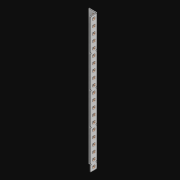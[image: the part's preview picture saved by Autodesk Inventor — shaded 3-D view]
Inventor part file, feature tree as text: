
AUTODESK INVENTOR PART (.ipt)
format: ipt  version: 2021 (Build 250183000, 183)  size: 1,229,824 bytes
history: native  units: in
note: dims shown in document units (in); Inventor stores cm internally (conversion verified against a paired STEP export)
features: extrude x44, other x42, sketch x4, pattern_linear x2, sheet_metal_op x1
ambient origin geometry x8: Origin, YZ Plane, XZ Plane, XY Plane, X Axis, Y Axis, Z Axis, Center Point
bodies: Solid1 (feature_tree)
feature tree (93):
  pattern_linear  "Rectangular Pattern1"  Spacing1=0.5in  [1 undecoded]
  pattern_linear  "Rectangular Pattern3"  Count1=21  [1 undecoded]
  extrude  "Extrusion1"  Depth=0.5in
  extrude  "Extrusion2"  Depth=0.5in
  sketch  "Sketch1"  dims[d0=0.182in]
  other  "Srf1"
  sketch  "Sketch3"  dims[d1=0.063in d2=0.0in]
  other  "Srf3"
  other  "Srf4"
  other  "Srf5"
  other  "Srf6"
  other  "Srf7"
  other  "Srf8"
  other  "Srf9"
  other  "Srf10"
  other  "Srf11"
  other  "Srf12"
  other  "Srf13"
  other  "Srf14"
  other  "Srf15"
  other  "Srf16"
  other  "Srf17"
  other  "Srf18"
  other  "Srf19"
  other  "Srf20"
  other  "Srf21"
  other  "Srf22"
  other  "Srf23"
  other  "Srf142"
  other  "Srf143"
  other  "Srf144"
  other  "Srf145"
  other  "Srf146"
  other  "Srf147"
  other  "Srf148"
  other  "Srf149"
  other  "Srf150"
  other  "Srf151"
  other  "Srf152"
  other  "Srf153"
  other  "Srf154"
  other  "Srf155"
  other  "Srf156"
  other  "Srf157"
  other  "Srf158"
  other  "Srf159"
  other  "Srf160"
  other  "Srf161"
  sketch  "Sketch4"  dims[d6=0.182in]
  sketch  "Sketch5"  dims[d7=0.063in d8=0.0in d11=0.5in d12=0.3937in d14=0.5in d18=8.2677in d20=0.5in d21=7.0in d22=0.0in d23=0.841in d24=0.0in]
  sheet_metal_op  "Fold1"
  extrude  "ExtrusionSrf1"  TaperAngle=0.0deg  [1 undecoded]
  extrude  "ExtrusionSrf3"  Depth=0.5in TaperAngle=0.0deg
  extrude  "ExtrusionSrf4"  [1 undecoded]
  extrude  "ExtrusionSrf5"  [1 undecoded]
  extrude  "ExtrusionSrf6"  [1 undecoded]
  extrude  "ExtrusionSrf7"  [1 undecoded]
  extrude  "ExtrusionSrf8"  [1 undecoded]
  extrude  "ExtrusionSrf9"  [1 undecoded]
  extrude  "ExtrusionSrf10"  [1 undecoded]
  extrude  "ExtrusionSrf11"  [1 undecoded]
  extrude  "ExtrusionSrf12"  [1 undecoded]
  extrude  "ExtrusionSrf13"  [1 undecoded]
  extrude  "ExtrusionSrf14"  [1 undecoded]
  extrude  "ExtrusionSrf15"  [1 undecoded]
  extrude  "ExtrusionSrf16"  [1 undecoded]
  extrude  "ExtrusionSrf17"  [1 undecoded]
  extrude  "ExtrusionSrf18"  [1 undecoded]
  extrude  "ExtrusionSrf19"  [1 undecoded]
  extrude  "ExtrusionSrf20"  [1 undecoded]
  extrude  "ExtrusionSrf21"  [1 undecoded]
  extrude  "ExtrusionSrf22"  [1 undecoded]
  extrude  "ExtrusionSrf23"  [1 undecoded]
  extrude  "ExtrusionSrf142"  [1 undecoded]
  extrude  "ExtrusionSrf143"  [1 undecoded]
  extrude  "ExtrusionSrf144"  [1 undecoded]
  extrude  "ExtrusionSrf145"  [1 undecoded]
  extrude  "ExtrusionSrf146"  [1 undecoded]
  extrude  "ExtrusionSrf147"  [1 undecoded]
  extrude  "ExtrusionSrf148"  [1 undecoded]
  extrude  "ExtrusionSrf149"  [1 undecoded]
  extrude  "ExtrusionSrf150"  [1 undecoded]
  extrude  "ExtrusionSrf151"  [1 undecoded]
  extrude  "ExtrusionSrf152"  [1 undecoded]
  extrude  "ExtrusionSrf153"  [1 undecoded]
  extrude  "ExtrusionSrf154"  [1 undecoded]
  extrude  "ExtrusionSrf155"  [1 undecoded]
  extrude  "ExtrusionSrf156"  [1 undecoded]
  extrude  "ExtrusionSrf157"  [1 undecoded]
  extrude  "ExtrusionSrf158"  [1 undecoded]
  extrude  "ExtrusionSrf159"  [1 undecoded]
  extrude  "ExtrusionSrf160"  [1 undecoded]
  extrude  "ExtrusionSrf161"  [1 undecoded]
note: 43 required parameter values undecoded (feature->parameter linkage not recoverable at this tier; creation-order binding heuristic only, values carry confidence <= 0.55)
